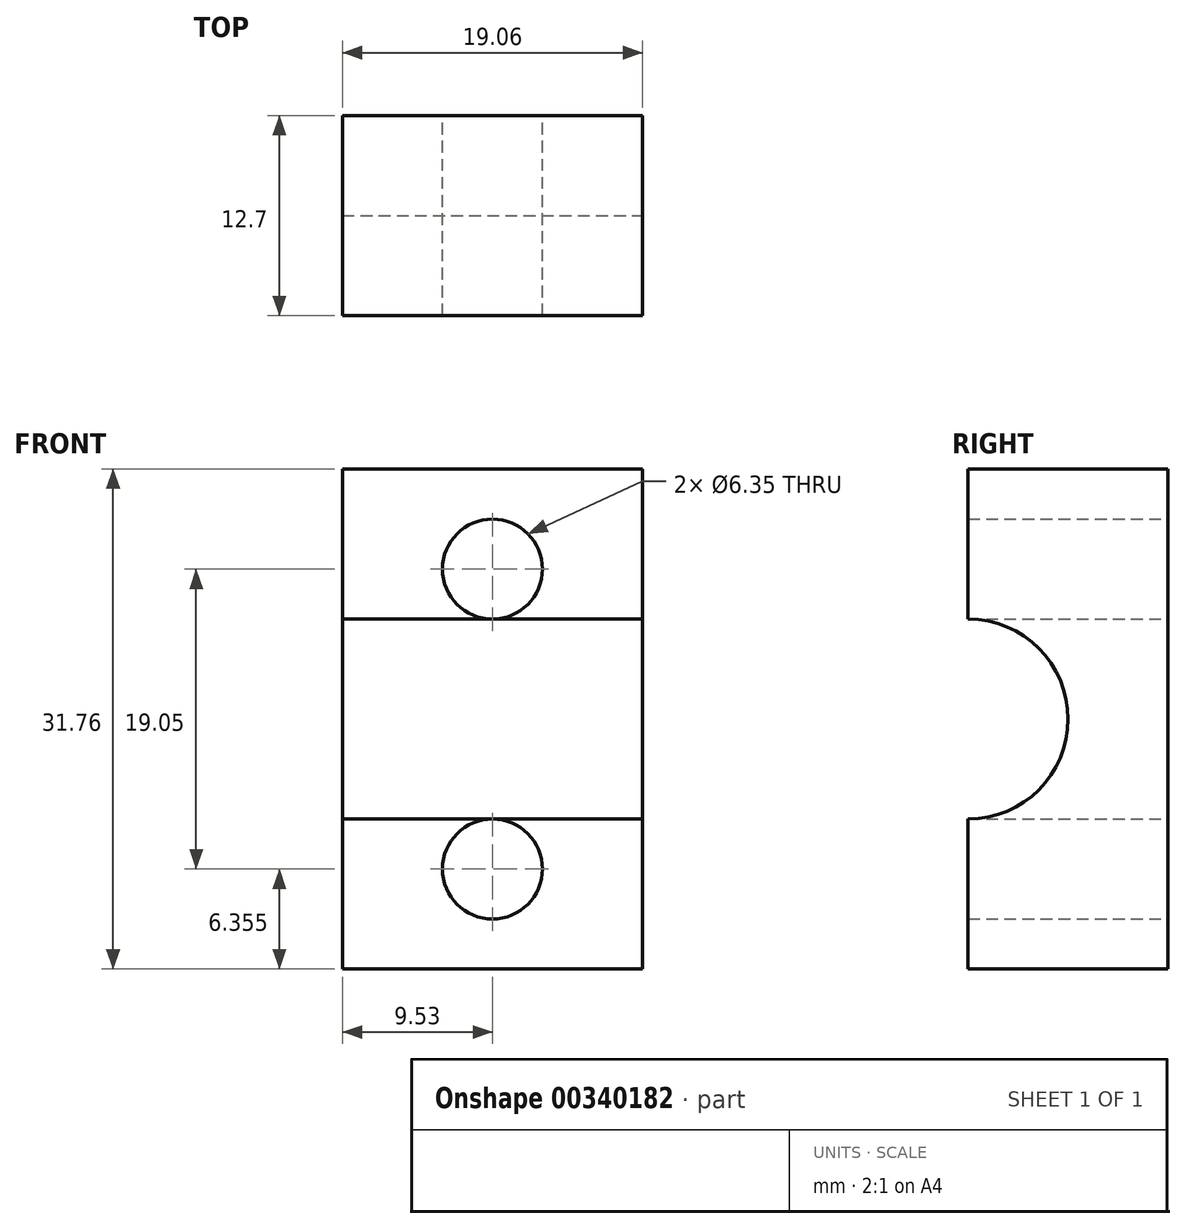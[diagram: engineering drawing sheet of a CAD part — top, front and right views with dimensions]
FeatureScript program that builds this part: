
annotation { "Feature Type Name" : "Feature", "Feature Type Description" : "" }
export const myFeature = defineFeature(function(context is Context, id is Id, definition is map)
    precondition{}
    {
        {
            var Q0;
            Q0=qCreatedBy(makeId("Front.planeOp"),FACE);
            var sketch = newSketch(context, id + "F0", { "sketchPlane" : qUnion([Q0])});
            skLineSegment(sketch, "E0.bottom", {"start": v(9.53, 15.88) * mm, "end": v(-9.53, 15.88) * mm});
            skLineSegment(sketch, "E0.top", {"start": v(9.53, -15.88) * mm, "end": v(-9.53, -15.88) * mm});
            skLineSegment(sketch, "E0.left", {"start": v(9.53, 15.88) * mm, "end": v(9.53, -15.88) * mm});
            skLineSegment(sketch, "E0.right", {"start": v(-9.53, 15.88) * mm, "end": v(-9.53, -15.88) * mm});
            skPoint(sketch, "E0.middle", {"position": v(0, 0) * mm});
            skLineSegment(sketch, "E1", {"start": v(0, 15.88) * mm, "end": v(0, -15.88) * mm, "construction": true});
            skCircle(sketch, "E2", {"center": v(0, 9.52) * mm, "radius": 3.18 * mm});
            skCircle(sketch, "E3", {"center": v(0, -9.52) * mm, "radius": 3.18 * mm});
            skSolve(sketch);
        }
        {
            var Q0;
            Q0 = qSketchRegion(id + "F0", true);
            extrude(context, id + "F1", {"entities" : qUnion([Q0]), "depth" : 12.7 * mm});
        }
        {
            var Q0;
            Q0=makeQuery(id+"F1.opExtrude","SWEPT_FACE",FACE,{"disambiguationData":[OSD([sQuery(id+"F0.wireOp",EDGE,"E0.left")])]});
            var sketch = newSketch(context, id + "F2", { "sketchPlane" : qUnion([Q0])});
            skCircle(sketch, "E4", {"center": v(-12.7, 0) * mm, "radius": 6.35 * mm});
            skSolve(sketch);
        }
        {
            var Q0;
            Q0 = qSketchRegion(id + "F2", true);
            extrude(context, id + "F3", {"entities" : qUnion([Q0]), "operationType" : NewBodyOperationType.REMOVE, "endBound" : BoundingType.THROUGH_ALL, "oppositeDirection" : true, "depth" : 25.4 * mm});
        }
    });
